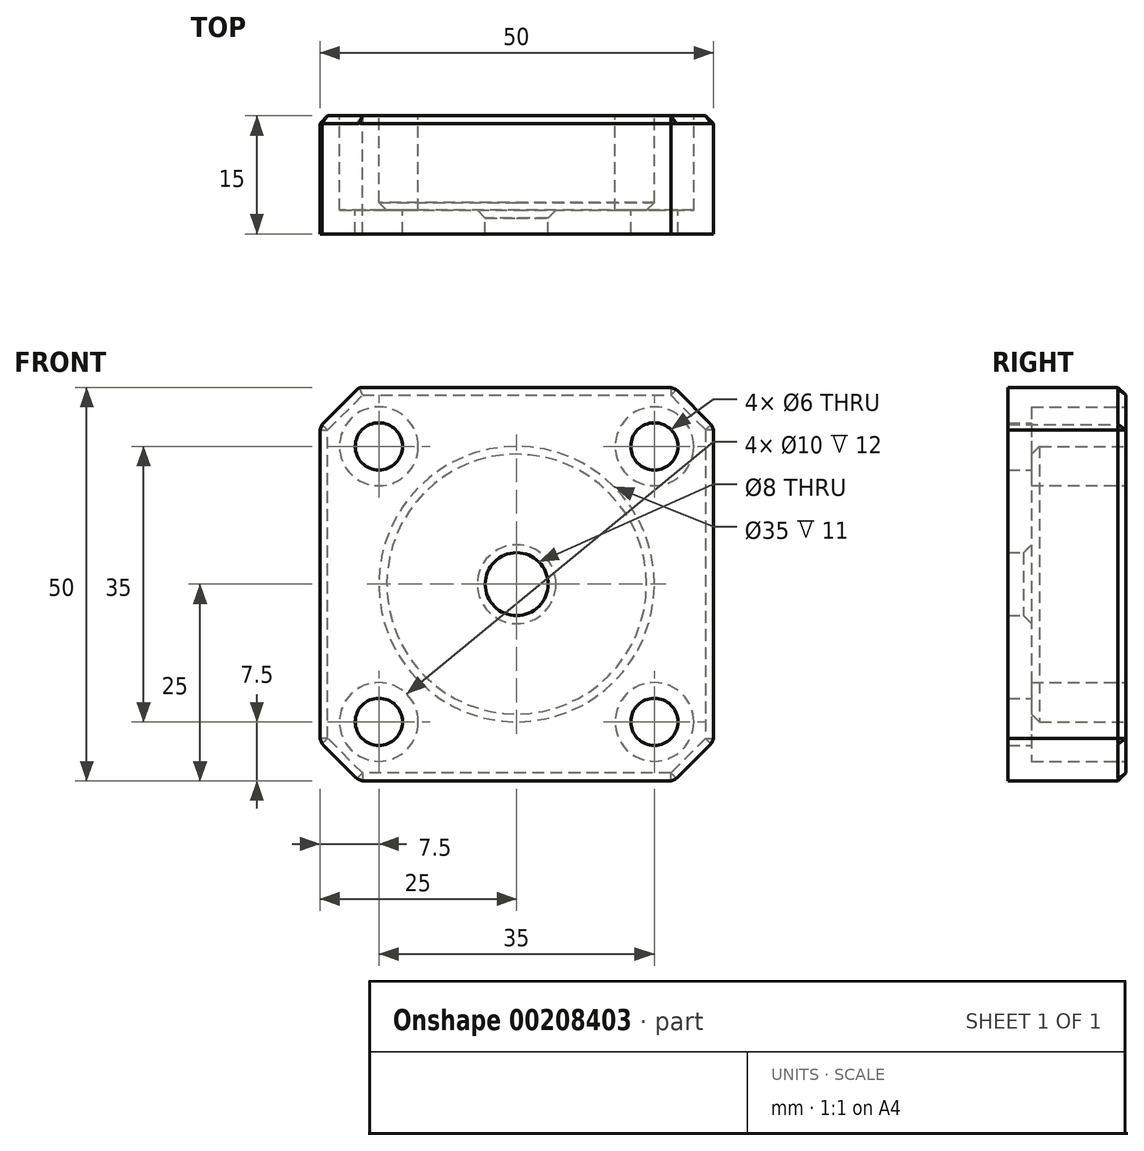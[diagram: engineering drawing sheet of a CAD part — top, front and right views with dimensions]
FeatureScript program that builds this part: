
annotation { "Feature Type Name" : "Feature", "Feature Type Description" : "" }
export const myFeature = defineFeature(function(context is Context, id is Id, definition is map)
    precondition{}
    {
        {
            var Q0;
            Q0=qCreatedBy(makeId("Front.planeOp"),FACE);
            var sketch = newSketch(context, id + "F6", { "sketchPlane" : qUnion([Q0])});
            skLineSegment(sketch, "E0.bottom", {"start": v(25, 25) * mm, "end": v(-25, 25) * mm});
            skLineSegment(sketch, "E0.top", {"start": v(25, -25) * mm, "end": v(-25, -25) * mm});
            skLineSegment(sketch, "E0.left", {"start": v(25, 25) * mm, "end": v(25, -25) * mm});
            skLineSegment(sketch, "E0.right", {"start": v(-25, 25) * mm, "end": v(-25, -25) * mm});
            skPoint(sketch, "E0.middle", {"position": v(0, 0) * mm});
            skCircle(sketch, "E1", {"center": v(0, 0) * mm, "radius": 4 * mm});
            skSolve(sketch);
        }
        {
            var Q0;
            Q0=makeQuery(id+"F6.imprint","IMPRINT",FACE,{"disambiguationData":[TD([[makeQuery(id+"F6.imprint","IMPRINT",EDGE,{"derivedFrom":sQuery(id+"F6.wireOp",EDGE,"E0.bottom")}),1.0]])]});
            extrude(context, id + "F7", {"entities" : qUnion([Q0]), "depth" : 15 * mm, "symmetric" : true});
        }
        {
            var Q0;
            Q0=makeQuery(id+"F7.opExtrude","SWEPT_EDGE",EDGE,{"disambiguationData":[OSD([sQuery(id+"F6.wireOp",EDGE,"E0.bottom"),sQuery(id+"F6.wireOp",EDGE,"E0.right")])]});
            var Q1;
            Q1=makeQuery(id+"F7.opExtrude","SWEPT_EDGE",EDGE,{"disambiguationData":[OSD([sQuery(id+"F6.wireOp",EDGE,"E0.bottom"),sQuery(id+"F6.wireOp",EDGE,"E0.left")])]});
            var Q2;
            Q2=makeQuery(id+"F7.opExtrude","SWEPT_EDGE",EDGE,{"disambiguationData":[OSD([sQuery(id+"F6.wireOp",EDGE,"E0.top"),sQuery(id+"F6.wireOp",EDGE,"E0.left")])]});
            var Q3;
            Q3=makeQuery(id+"F7.opExtrude","SWEPT_EDGE",EDGE,{"disambiguationData":[OSD([sQuery(id+"F6.wireOp",EDGE,"E0.top"),sQuery(id+"F6.wireOp",EDGE,"E0.right")])]});
            chamfer(context, id + "F8", {"entities" : qUnion([Q0, Q1, Q2, Q3]), "width" : 5 * mm, "tangentPropagation" : true});
        }
        {
            var Q0;
            Q0=makeQuery(id+"F7.opExtrude","CAP_FACE",FACE,{"disambiguationData":[OSD([sQuery(id+"F6.wireOp",EDGE,"E0.bottom"),sQuery(id+"F6.wireOp",EDGE,"E0.top"),sQuery(id+"F6.wireOp",EDGE,"E0.left"),sQuery(id+"F6.wireOp",EDGE,"E0.right"),sQuery(id+"F6.wireOp",EDGE,"E1")])],"isStart":true});
            var sketch = newSketch(context, id + "F0", { "sketchPlane" : qUnion([Q0])});
            skCircle(sketch, "E2", {"center": v(0, 0) * mm, "radius": 17.5 * mm});
            skCircle(sketch, "E3", {"center": v(17.5, -17.5) * mm, "radius": 3 * mm});
            skCircle(sketch, "E4", {"center": v(17.5, 17.5) * mm, "radius": 3 * mm});
            skCircle(sketch, "E5", {"center": v(-17.5, -17.5) * mm, "radius": 3 * mm});
            skCircle(sketch, "E6", {"center": v(-17.5, 17.5) * mm, "radius": 3 * mm});
            skCircle(sketch, "E7", {"center": v(-17.5, 17.5) * mm, "radius": 5 * mm});
            skCircle(sketch, "E8", {"center": v(17.5, -17.5) * mm, "radius": 5 * mm});
            skCircle(sketch, "E9", {"center": v(-17.5, -17.5) * mm, "radius": 5 * mm});
            skCircle(sketch, "E10", {"center": v(17.5, 17.5) * mm, "radius": 5 * mm});
            skSolve(sketch);
        }
        {
            var Q0;
            Q0=makeQuery(id+"F0.imprint","IMPRINT",FACE,{"disambiguationData":[TD([[makeQuery(id+"F0.imprint","IMPRINT",EDGE,{"derivedFrom":sQuery(id+"F0.wireOp",EDGE,"E2")}),1.0]])]});
            extrude(context, id + "F1", {"entities" : qUnion([Q0]), "operationType" : NewBodyOperationType.REMOVE, "oppositeDirection" : true, "depth" : 12 * mm});
        }
        {
            var Q0;
            Q0=makeQuery(id+"F0.imprint","IMPRINT",FACE,{"disambiguationData":[TD([[makeQuery(id+"F0.imprint","IMPRINT",EDGE,{"derivedFrom":sQuery(id+"F0.wireOp",EDGE,"E6")}),1.0]])]});
            var Q1;
            Q1=makeQuery(id+"F0.imprint","IMPRINT",FACE,{"disambiguationData":[TD([[makeQuery(id+"F0.imprint","IMPRINT",EDGE,{"derivedFrom":sQuery(id+"F0.wireOp",EDGE,"E5")}),1.0]])]});
            var Q2;
            Q2=makeQuery(id+"F0.imprint","IMPRINT",FACE,{"disambiguationData":[TD([[makeQuery(id+"F0.imprint","IMPRINT",EDGE,{"derivedFrom":sQuery(id+"F0.wireOp",EDGE,"E3")}),1.0]])]});
            var Q3;
            Q3=makeQuery(id+"F0.imprint","IMPRINT",FACE,{"disambiguationData":[TD([[makeQuery(id+"F0.imprint","IMPRINT",EDGE,{"derivedFrom":sQuery(id+"F0.wireOp",EDGE,"E4")}),1.0]])]});
            var Q4;
            Q4=sQuery(id+"F0.wireOp",EDGE,"E6");
            var Q5;
            Q5=sQuery(id+"F0.wireOp",EDGE,"E5");
            var Q6;
            Q6=sQuery(id+"F0.wireOp",EDGE,"E3");
            var Q7;
            Q7=sQuery(id+"F0.wireOp",EDGE,"E4");
            extrude(context, id + "F2", {"entities" : qUnion([Q0, Q1, Q2, Q3]), "operationType" : NewBodyOperationType.REMOVE, "surfaceEntities" : qUnion([Q4, Q5, Q6, Q7]), "oppositeDirection" : true, "depth" : 15 * mm});
        }
        {
            var Q0;
            Q0=makeQuery(id+"F0.imprint","IMPRINT",FACE,{"disambiguationData":[TD([[makeQuery(id+"F0.imprint","IMPRINT",EDGE,{"derivedFrom":sQuery(id+"F0.wireOp",EDGE,"E6")}),-1.0]])]});
            var Q1;
            Q1=makeQuery(id+"F0.imprint","IMPRINT",FACE,{"disambiguationData":[TD([[makeQuery(id+"F0.imprint","IMPRINT",EDGE,{"derivedFrom":sQuery(id+"F0.wireOp",EDGE,"E5")}),-1.0]])]});
            var Q2;
            Q2=makeQuery(id+"F0.imprint","IMPRINT",FACE,{"disambiguationData":[TD([[makeQuery(id+"F0.imprint","IMPRINT",EDGE,{"derivedFrom":sQuery(id+"F0.wireOp",EDGE,"E3")}),-1.0]])]});
            var Q3;
            Q3=makeQuery(id+"F0.imprint","IMPRINT",FACE,{"disambiguationData":[TD([[makeQuery(id+"F0.imprint","IMPRINT",EDGE,{"derivedFrom":sQuery(id+"F0.wireOp",EDGE,"E4")}),-1.0]])]});
            extrude(context, id + "F3", {"entities" : qUnion([Q0, Q1, Q2, Q3]), "operationType" : NewBodyOperationType.REMOVE, "oppositeDirection" : true, "depth" : 12 * mm});
        }
        {
            var Q0;
            Q0=makeQuery(id+"F7.opExtrude","CAP_EDGE",EDGE,{"disambiguationData":[OSD([sQuery(id+"F6.wireOp",EDGE,"E0.left")])],"isStart":true});
            var Q1;
            {var subQ0=sQuery(id+"F6.wireOp",EDGE,"E0.left");var subQ1=sQuery(id+"F6.wireOp",EDGE,"E0.bottom");Q1=makeQuery(id+"F8.opChamfer","BLEND_EDGE",EDGE,{"blendedFrom":[makeQuery(id+"F7.opExtrude","SWEPT_EDGE",EDGE,{"disambiguationData":[OSD([subQ1,subQ0])]}),makeQuery(id+"F7.opExtrude","CAP_FACE",FACE,{"disambiguationData":[OSD([subQ1,sQuery(id+"F6.wireOp",EDGE,"E0.top"),subQ0,sQuery(id+"F6.wireOp",EDGE,"E0.right"),sQuery(id+"F6.wireOp",EDGE,"E1")])],"isStart":true})],"blendedInto":[makeQuery(id+"F7.opExtrude","CAP_FACE",FACE,{"disambiguationData":[OSD([subQ1,sQuery(id+"F6.wireOp",EDGE,"E0.top"),subQ0,sQuery(id+"F6.wireOp",EDGE,"E0.right"),sQuery(id+"F6.wireOp",EDGE,"E1")])],"isStart":true})]});}
            var Q2;
            Q2=makeQuery(id+"F7.opExtrude","CAP_EDGE",EDGE,{"disambiguationData":[OSD([sQuery(id+"F6.wireOp",EDGE,"E0.bottom")])],"isStart":true});
            var Q3;
            {var subQ0=sQuery(id+"F6.wireOp",EDGE,"E0.left");var subQ1=sQuery(id+"F6.wireOp",EDGE,"E0.top");Q3=makeQuery(id+"F8.opChamfer","BLEND_EDGE",EDGE,{"blendedFrom":[makeQuery(id+"F7.opExtrude","SWEPT_EDGE",EDGE,{"disambiguationData":[OSD([subQ1,subQ0])]}),makeQuery(id+"F7.opExtrude","CAP_FACE",FACE,{"disambiguationData":[OSD([sQuery(id+"F6.wireOp",EDGE,"E0.bottom"),subQ1,subQ0,sQuery(id+"F6.wireOp",EDGE,"E0.right"),sQuery(id+"F6.wireOp",EDGE,"E1")])],"isStart":true})],"blendedInto":[makeQuery(id+"F7.opExtrude","CAP_FACE",FACE,{"disambiguationData":[OSD([sQuery(id+"F6.wireOp",EDGE,"E0.bottom"),subQ1,subQ0,sQuery(id+"F6.wireOp",EDGE,"E0.right"),sQuery(id+"F6.wireOp",EDGE,"E1")])],"isStart":true})]});}
            var Q4;
            Q4=makeQuery(id+"F7.opExtrude","CAP_EDGE",EDGE,{"disambiguationData":[OSD([sQuery(id+"F6.wireOp",EDGE,"E0.top")])],"isStart":true});
            var Q5;
            {var subQ0=sQuery(id+"F6.wireOp",EDGE,"E0.right");var subQ1=sQuery(id+"F6.wireOp",EDGE,"E0.top");Q5=makeQuery(id+"F8.opChamfer","BLEND_EDGE",EDGE,{"blendedFrom":[makeQuery(id+"F7.opExtrude","SWEPT_EDGE",EDGE,{"disambiguationData":[OSD([subQ1,subQ0])]}),makeQuery(id+"F7.opExtrude","CAP_FACE",FACE,{"disambiguationData":[OSD([sQuery(id+"F6.wireOp",EDGE,"E0.bottom"),subQ1,sQuery(id+"F6.wireOp",EDGE,"E0.left"),subQ0,sQuery(id+"F6.wireOp",EDGE,"E1")])],"isStart":true})],"blendedInto":[makeQuery(id+"F7.opExtrude","CAP_FACE",FACE,{"disambiguationData":[OSD([sQuery(id+"F6.wireOp",EDGE,"E0.bottom"),subQ1,sQuery(id+"F6.wireOp",EDGE,"E0.left"),subQ0,sQuery(id+"F6.wireOp",EDGE,"E1")])],"isStart":true})]});}
            var Q6;
            Q6=makeQuery(id+"F7.opExtrude","CAP_EDGE",EDGE,{"disambiguationData":[OSD([sQuery(id+"F6.wireOp",EDGE,"E0.right")])],"isStart":true});
            var Q7;
            {var subQ0=sQuery(id+"F6.wireOp",EDGE,"E0.right");var subQ1=sQuery(id+"F6.wireOp",EDGE,"E0.bottom");Q7=makeQuery(id+"F8.opChamfer","BLEND_EDGE",EDGE,{"blendedFrom":[makeQuery(id+"F7.opExtrude","SWEPT_EDGE",EDGE,{"disambiguationData":[OSD([subQ1,subQ0])]}),makeQuery(id+"F7.opExtrude","CAP_FACE",FACE,{"disambiguationData":[OSD([subQ1,sQuery(id+"F6.wireOp",EDGE,"E0.top"),sQuery(id+"F6.wireOp",EDGE,"E0.left"),subQ0,sQuery(id+"F6.wireOp",EDGE,"E1")])],"isStart":true})],"blendedInto":[makeQuery(id+"F7.opExtrude","CAP_FACE",FACE,{"disambiguationData":[OSD([subQ1,sQuery(id+"F6.wireOp",EDGE,"E0.top"),sQuery(id+"F6.wireOp",EDGE,"E0.left"),subQ0,sQuery(id+"F6.wireOp",EDGE,"E1")])],"isStart":true})]});}
            var Q8;
            Q8=makeQuery(id+"F3.boolean.opBoolean","COPY",EDGE,{"derivedFrom":makeQuery(id+"F3.opExtrude","CAP_EDGE",EDGE,{"disambiguationData":[OSD([sQuery(id+"F0.wireOp",EDGE,"E10")])],"isStart":true})});
            var Q9;
            Q9=makeQuery(id+"F3.boolean.opBoolean","COPY",EDGE,{"derivedFrom":makeQuery(id+"F3.opExtrude","CAP_EDGE",EDGE,{"disambiguationData":[OSD([sQuery(id+"F0.wireOp",EDGE,"E8")])],"isStart":true})});
            var Q10;
            Q10=makeQuery(id+"F1.boolean.opBoolean","COPY",EDGE,{"derivedFrom":makeQuery(id+"F1.opExtrude","CAP_EDGE",EDGE,{"disambiguationData":[OSD([sQuery(id+"F0.wireOp",EDGE,"E2")])],"isStart":true})});
            var Q11;
            Q11=makeQuery(id+"F1.boolean.opBoolean","COPY",FACE,{"derivedFrom":makeQuery(id+"F1.opExtrude","CAP_FACE",FACE,{"disambiguationData":[OSD([sQuery(id+"F6.wireOp",EDGE,"E1"),sQuery(id+"F0.wireOp",EDGE,"E2")])],"isStart":false})});
            var Q12;
            Q12=makeQuery(id+"F3.boolean.opBoolean","COPY",EDGE,{"derivedFrom":makeQuery(id+"F3.opExtrude","CAP_EDGE",EDGE,{"disambiguationData":[OSD([sQuery(id+"F0.wireOp",EDGE,"E9")])],"isStart":true})});
            var Q13;
            Q13=makeQuery(id+"F3.boolean.opBoolean","COPY",EDGE,{"derivedFrom":makeQuery(id+"F3.opExtrude","CAP_EDGE",EDGE,{"disambiguationData":[OSD([sQuery(id+"F0.wireOp",EDGE,"E5")])],"isStart":false})});
            var Q14;
            Q14=makeQuery(id+"F3.boolean.opBoolean","COPY",EDGE,{"derivedFrom":makeQuery(id+"F3.opExtrude","CAP_EDGE",EDGE,{"disambiguationData":[OSD([sQuery(id+"F0.wireOp",EDGE,"E7")])],"isStart":true})});
            var Q15;
            Q15=makeQuery(id+"F3.boolean.opBoolean","COPY",EDGE,{"derivedFrom":makeQuery(id+"F3.opExtrude","CAP_EDGE",EDGE,{"disambiguationData":[OSD([sQuery(id+"F0.wireOp",EDGE,"E6")])],"isStart":false})});
            var Q16;
            Q16=makeQuery(id+"F3.boolean.opBoolean","COPY",EDGE,{"derivedFrom":makeQuery(id+"F3.opExtrude","CAP_EDGE",EDGE,{"disambiguationData":[OSD([sQuery(id+"F0.wireOp",EDGE,"E4")])],"isStart":false})});
            var Q17;
            Q17=makeQuery(id+"F3.boolean.opBoolean","COPY",EDGE,{"derivedFrom":makeQuery(id+"F3.opExtrude","CAP_EDGE",EDGE,{"disambiguationData":[OSD([sQuery(id+"F0.wireOp",EDGE,"E3")])],"isStart":false})});
            var Q18;
            {var subQ0=sQuery(id+"F6.wireOp",EDGE,"E0.left");Q18=makeQuery(id+"F8.opChamfer","BLEND_EDGE",EDGE,{"blendedFrom":[makeQuery(id+"F7.opExtrude","SWEPT_EDGE",EDGE,{"disambiguationData":[OSD([sQuery(id+"F6.wireOp",EDGE,"E0.top"),subQ0])]}),makeQuery(id+"F7.opExtrude","SWEPT_FACE",FACE,{"disambiguationData":[OSD([subQ0])]})],"blendedInto":[makeQuery(id+"F7.opExtrude","SWEPT_FACE",FACE,{"disambiguationData":[OSD([subQ0])]})]});}
            var Q19;
            {var subQ0=sQuery(id+"F6.wireOp",EDGE,"E0.left");Q19=makeQuery(id+"F8.opChamfer","BLEND_EDGE",EDGE,{"blendedFrom":[makeQuery(id+"F7.opExtrude","SWEPT_EDGE",EDGE,{"disambiguationData":[OSD([sQuery(id+"F6.wireOp",EDGE,"E0.bottom"),subQ0])]}),makeQuery(id+"F7.opExtrude","SWEPT_FACE",FACE,{"disambiguationData":[OSD([subQ0])]})],"blendedInto":[makeQuery(id+"F7.opExtrude","SWEPT_FACE",FACE,{"disambiguationData":[OSD([subQ0])]})]});}
            var Q20;
            {var subQ0=sQuery(id+"F6.wireOp",EDGE,"E0.bottom");Q20=makeQuery(id+"F8.opChamfer","BLEND_EDGE",EDGE,{"blendedFrom":[makeQuery(id+"F7.opExtrude","SWEPT_EDGE",EDGE,{"disambiguationData":[OSD([subQ0,sQuery(id+"F6.wireOp",EDGE,"E0.left")])]}),makeQuery(id+"F7.opExtrude","SWEPT_FACE",FACE,{"disambiguationData":[OSD([subQ0])]})],"blendedInto":[makeQuery(id+"F7.opExtrude","SWEPT_FACE",FACE,{"disambiguationData":[OSD([subQ0])]})]});}
            var Q21;
            {var subQ0=sQuery(id+"F6.wireOp",EDGE,"E0.top");Q21=makeQuery(id+"F8.opChamfer","BLEND_EDGE",EDGE,{"blendedFrom":[makeQuery(id+"F7.opExtrude","SWEPT_EDGE",EDGE,{"disambiguationData":[OSD([subQ0,sQuery(id+"F6.wireOp",EDGE,"E0.left")])]}),makeQuery(id+"F7.opExtrude","SWEPT_FACE",FACE,{"disambiguationData":[OSD([subQ0])]})],"blendedInto":[makeQuery(id+"F7.opExtrude","SWEPT_FACE",FACE,{"disambiguationData":[OSD([subQ0])]})]});}
            var Q22;
            {var subQ0=sQuery(id+"F6.wireOp",EDGE,"E0.right");Q22=makeQuery(id+"F8.opChamfer","BLEND_EDGE",EDGE,{"blendedFrom":[makeQuery(id+"F7.opExtrude","SWEPT_EDGE",EDGE,{"disambiguationData":[OSD([sQuery(id+"F6.wireOp",EDGE,"E0.bottom"),subQ0])]}),makeQuery(id+"F7.opExtrude","SWEPT_FACE",FACE,{"disambiguationData":[OSD([subQ0])]})],"blendedInto":[makeQuery(id+"F7.opExtrude","SWEPT_FACE",FACE,{"disambiguationData":[OSD([subQ0])]})]});}
            var Q23;
            {var subQ0=sQuery(id+"F6.wireOp",EDGE,"E0.right");Q23=makeQuery(id+"F8.opChamfer","BLEND_EDGE",EDGE,{"blendedFrom":[makeQuery(id+"F7.opExtrude","SWEPT_EDGE",EDGE,{"disambiguationData":[OSD([sQuery(id+"F6.wireOp",EDGE,"E0.top"),subQ0])]}),makeQuery(id+"F7.opExtrude","SWEPT_FACE",FACE,{"disambiguationData":[OSD([subQ0])]})],"blendedInto":[makeQuery(id+"F7.opExtrude","SWEPT_FACE",FACE,{"disambiguationData":[OSD([subQ0])]})]});}
            var Q24;
            {var subQ0=sQuery(id+"F6.wireOp",EDGE,"E0.top");Q24=makeQuery(id+"F8.opChamfer","BLEND_EDGE",EDGE,{"blendedFrom":[makeQuery(id+"F7.opExtrude","SWEPT_EDGE",EDGE,{"disambiguationData":[OSD([subQ0,sQuery(id+"F6.wireOp",EDGE,"E0.right")])]}),makeQuery(id+"F7.opExtrude","SWEPT_FACE",FACE,{"disambiguationData":[OSD([subQ0])]})],"blendedInto":[makeQuery(id+"F7.opExtrude","SWEPT_FACE",FACE,{"disambiguationData":[OSD([subQ0])]})]});}
            chamfer(context, id + "F4", {"entities" : qUnion([Q0, Q1, Q2, Q3, Q4, Q5, Q6, Q7, Q8, Q9, Q10, Q11, Q12, Q13, Q14, Q15, Q16, Q17, Q18, Q19, Q20, Q21, Q22, Q23, Q24]), "width" : 1 * mm, "tangentPropagation" : true});
        }
        {
            var Q0;
            {var subQ0=sQuery(id+"F6.wireOp",EDGE,"E0.bottom");Q0=makeQuery(id+"F8.opChamfer","BLEND_EDGE",EDGE,{"blendedFrom":[makeQuery(id+"F7.opExtrude","SWEPT_EDGE",EDGE,{"disambiguationData":[OSD([subQ0,sQuery(id+"F6.wireOp",EDGE,"E0.right")])]}),makeQuery(id+"F7.opExtrude","SWEPT_FACE",FACE,{"disambiguationData":[OSD([subQ0])]})],"blendedInto":[makeQuery(id+"F7.opExtrude","SWEPT_FACE",FACE,{"disambiguationData":[OSD([subQ0])]})]});}
            var Q1;
            {var subQ0=sQuery(id+"F6.wireOp",EDGE,"E0.right");var subQ1=sQuery(id+"F6.wireOp",EDGE,"E0.top");Q1=makeQuery(id+"F4.opChamfer","BLEND_EDGE",EDGE,{"blendedFrom":[makeQuery(id+"F8.opChamfer","BLEND_EDGE",EDGE,{"blendedFrom":[makeQuery(id+"F7.opExtrude","SWEPT_EDGE",EDGE,{"disambiguationData":[OSD([subQ1,subQ0])]}),makeQuery(id+"F7.opExtrude","SWEPT_FACE",FACE,{"disambiguationData":[OSD([subQ0])]})],"blendedInto":[makeQuery(id+"F7.opExtrude","SWEPT_FACE",FACE,{"disambiguationData":[OSD([subQ0])]})]}),makeQuery(id+"F8.opChamfer","BLEND_FACE",FACE,{"disambiguationData":[OSD([subQ1,subQ0])]})],"blendedInto":[makeQuery(id+"F8.opChamfer","BLEND_FACE",FACE,{"disambiguationData":[OSD([subQ1,subQ0])]})]});}
            var Q2;
            {var subQ0=sQuery(id+"F6.wireOp",EDGE,"E0.right");var subQ1=sQuery(id+"F6.wireOp",EDGE,"E0.top");Q2=makeQuery(id+"F4.opChamfer","BLEND_EDGE",EDGE,{"blendedFrom":[makeQuery(id+"F8.opChamfer","BLEND_EDGE",EDGE,{"blendedFrom":[makeQuery(id+"F7.opExtrude","SWEPT_EDGE",EDGE,{"disambiguationData":[OSD([subQ1,subQ0])]}),makeQuery(id+"F7.opExtrude","SWEPT_FACE",FACE,{"disambiguationData":[OSD([subQ1])]})],"blendedInto":[makeQuery(id+"F7.opExtrude","SWEPT_FACE",FACE,{"disambiguationData":[OSD([subQ1])]})]}),makeQuery(id+"F8.opChamfer","BLEND_FACE",FACE,{"disambiguationData":[OSD([subQ1,subQ0])]})],"blendedInto":[makeQuery(id+"F8.opChamfer","BLEND_FACE",FACE,{"disambiguationData":[OSD([subQ1,subQ0])]})]});}
            var Q3;
            {var subQ0=sQuery(id+"F6.wireOp",EDGE,"E0.left");var subQ1=sQuery(id+"F6.wireOp",EDGE,"E0.top");Q3=makeQuery(id+"F4.opChamfer","BLEND_EDGE",EDGE,{"blendedFrom":[makeQuery(id+"F8.opChamfer","BLEND_EDGE",EDGE,{"blendedFrom":[makeQuery(id+"F7.opExtrude","SWEPT_EDGE",EDGE,{"disambiguationData":[OSD([subQ1,subQ0])]}),makeQuery(id+"F7.opExtrude","SWEPT_FACE",FACE,{"disambiguationData":[OSD([subQ1])]})],"blendedInto":[makeQuery(id+"F7.opExtrude","SWEPT_FACE",FACE,{"disambiguationData":[OSD([subQ1])]})]}),makeQuery(id+"F8.opChamfer","BLEND_FACE",FACE,{"disambiguationData":[OSD([subQ1,subQ0])]})],"blendedInto":[makeQuery(id+"F8.opChamfer","BLEND_FACE",FACE,{"disambiguationData":[OSD([subQ1,subQ0])]})]});}
            var Q4;
            {var subQ0=sQuery(id+"F6.wireOp",EDGE,"E0.left");var subQ1=sQuery(id+"F6.wireOp",EDGE,"E0.top");Q4=makeQuery(id+"F4.opChamfer","BLEND_EDGE",EDGE,{"blendedFrom":[makeQuery(id+"F8.opChamfer","BLEND_EDGE",EDGE,{"blendedFrom":[makeQuery(id+"F7.opExtrude","SWEPT_EDGE",EDGE,{"disambiguationData":[OSD([subQ1,subQ0])]}),makeQuery(id+"F7.opExtrude","SWEPT_FACE",FACE,{"disambiguationData":[OSD([subQ0])]})],"blendedInto":[makeQuery(id+"F7.opExtrude","SWEPT_FACE",FACE,{"disambiguationData":[OSD([subQ0])]})]}),makeQuery(id+"F8.opChamfer","BLEND_FACE",FACE,{"disambiguationData":[OSD([subQ1,subQ0])]})],"blendedInto":[makeQuery(id+"F8.opChamfer","BLEND_FACE",FACE,{"disambiguationData":[OSD([subQ1,subQ0])]})]});}
            var Q5;
            {var subQ0=sQuery(id+"F6.wireOp",EDGE,"E0.left");var subQ1=sQuery(id+"F6.wireOp",EDGE,"E0.bottom");Q5=makeQuery(id+"F4.opChamfer","BLEND_EDGE",EDGE,{"blendedFrom":[makeQuery(id+"F8.opChamfer","BLEND_EDGE",EDGE,{"blendedFrom":[makeQuery(id+"F7.opExtrude","SWEPT_EDGE",EDGE,{"disambiguationData":[OSD([subQ1,subQ0])]}),makeQuery(id+"F7.opExtrude","SWEPT_FACE",FACE,{"disambiguationData":[OSD([subQ0])]})],"blendedInto":[makeQuery(id+"F7.opExtrude","SWEPT_FACE",FACE,{"disambiguationData":[OSD([subQ0])]})]}),makeQuery(id+"F8.opChamfer","BLEND_FACE",FACE,{"disambiguationData":[OSD([subQ1,subQ0])]})],"blendedInto":[makeQuery(id+"F8.opChamfer","BLEND_FACE",FACE,{"disambiguationData":[OSD([subQ1,subQ0])]})]});}
            var Q6;
            {var subQ0=sQuery(id+"F6.wireOp",EDGE,"E0.left");var subQ1=sQuery(id+"F6.wireOp",EDGE,"E0.bottom");Q6=makeQuery(id+"F4.opChamfer","BLEND_EDGE",EDGE,{"blendedFrom":[makeQuery(id+"F8.opChamfer","BLEND_EDGE",EDGE,{"blendedFrom":[makeQuery(id+"F7.opExtrude","SWEPT_EDGE",EDGE,{"disambiguationData":[OSD([subQ1,subQ0])]}),makeQuery(id+"F7.opExtrude","SWEPT_FACE",FACE,{"disambiguationData":[OSD([subQ1])]})],"blendedInto":[makeQuery(id+"F7.opExtrude","SWEPT_FACE",FACE,{"disambiguationData":[OSD([subQ1])]})]}),makeQuery(id+"F8.opChamfer","BLEND_FACE",FACE,{"disambiguationData":[OSD([subQ1,subQ0])]})],"blendedInto":[makeQuery(id+"F8.opChamfer","BLEND_FACE",FACE,{"disambiguationData":[OSD([subQ1,subQ0])]})]});}
            fillet(context, id + "F5", {"entities" : qUnion([Q0, Q1, Q2, Q3, Q4, Q5, Q6]), "radius" : 1 * mm, "tangentPropagation" : true, "allowEdgeOverflow" : false});
        }
    });
